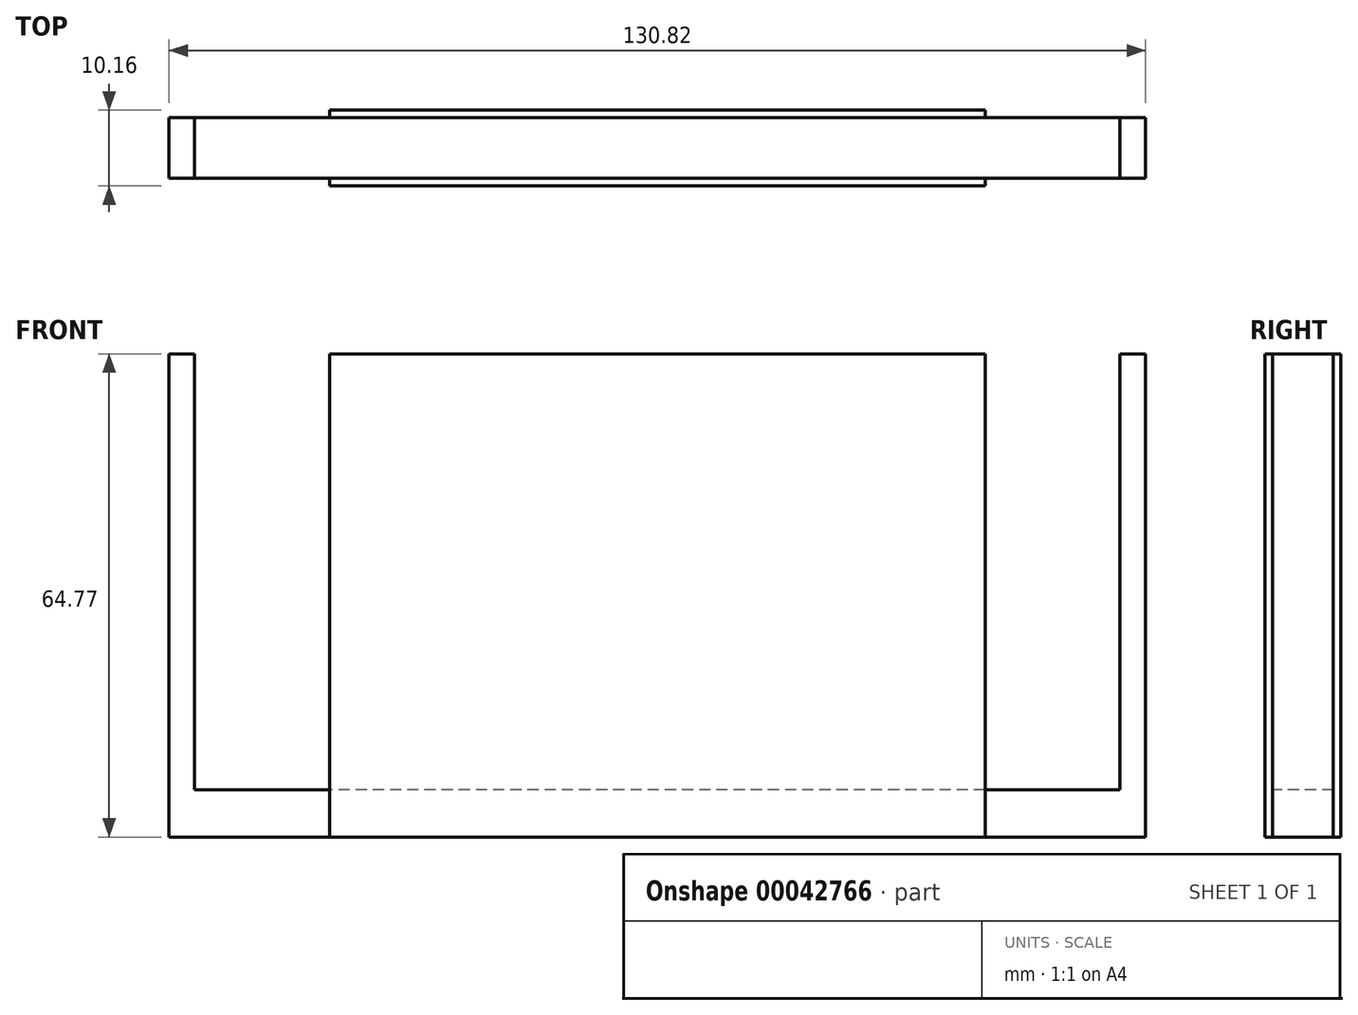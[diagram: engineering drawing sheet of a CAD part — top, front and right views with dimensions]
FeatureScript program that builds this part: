
annotation { "Feature Type Name" : "Feature", "Feature Type Description" : "" }
export const myFeature = defineFeature(function(context is Context, id is Id, definition is map)
    precondition{}
    {
        {
            var Q0;
            Q0=qCreatedBy(makeId("Top.planeOp"),FACE);
            var sketch = newSketch(context, id + "F0", { "sketchPlane" : qUnion([Q0])});
            skLineSegment(sketch, "E0.rect.bottom", {"start": v(61.98, 4.06) * mm, "end": v(-61.98, 4.06) * mm});
            skLineSegment(sketch, "E0.rect.top", {"start": v(61.98, -4.06) * mm, "end": v(-61.98, -4.06) * mm});
            skLineSegment(sketch, "E0.rect.left", {"start": v(61.98, 4.06) * mm, "end": v(61.98, -4.06) * mm});
            skLineSegment(sketch, "E0.rect.right", {"start": v(-61.98, 4.06) * mm, "end": v(-61.98, -4.06) * mm});
            skPoint(sketch, "E0.rect.middle", {"position": v(0, 0) * mm});
            skLineSegment(sketch, "E1.rect.bottom", {"start": v(43.9, 5.08) * mm, "end": v(-43.9, 5.08) * mm});
            skLineSegment(sketch, "E1.rect.top", {"start": v(43.9, -5.08) * mm, "end": v(-43.9, -5.08) * mm});
            skLineSegment(sketch, "E1.rect.left", {"start": v(43.9, 5.08) * mm, "end": v(43.9, -5.08) * mm});
            skLineSegment(sketch, "E1.rect.right", {"start": v(-43.9, 5.08) * mm, "end": v(-43.9, -5.08) * mm});
            skLineSegment(sketch, "E2.rect.bottom", {"start": v(65.41, 4.06) * mm, "end": v(-65.41, 4.06) * mm});
            skLineSegment(sketch, "E2.rect.top", {"start": v(65.41, -4.06) * mm, "end": v(-65.41, -4.06) * mm});
            skLineSegment(sketch, "E2.rect.left", {"start": v(65.41, 4.06) * mm, "end": v(65.41, -4.06) * mm});
            skLineSegment(sketch, "E2.rect.right", {"start": v(-65.41, 4.06) * mm, "end": v(-65.41, -4.06) * mm});
            skSolve(sketch);
        }
        {
            var Q0;
            {var subQ0=sQuery(id+"F0.wireOp",EDGE,"E0.rect.right");Q0=makeQuery(id+"F0.imprint","IMPRINT",FACE,{"disambiguationData":[TD([[makeQuery(id+"F0.imprint","IMPRINT",EDGE,{"derivedFrom":subQ0}),-1.0]])]});}
            var Q1;
            {var subQ0=sQuery(id+"F0.wireOp",EDGE,"E1.rect.bottom");Q1=makeQuery(id+"F0.imprint","IMPRINT",FACE,{"disambiguationData":[TD([[makeQuery(id+"F0.imprint","IMPRINT",EDGE,{"derivedFrom":subQ0}),1.0]])]});}
            var Q2;
            {var subQ0=sQuery(id+"F0.wireOp",EDGE,"E1.rect.top");Q2=makeQuery(id+"F0.imprint","IMPRINT",FACE,{"disambiguationData":[TD([[makeQuery(id+"F0.imprint","IMPRINT",EDGE,{"derivedFrom":subQ0}),-1.0]])]});}
            var Q3;
            {var subQ0=sQuery(id+"F0.wireOp",EDGE,"E0.rect.right");Q3=makeQuery(id+"F0.imprint","IMPRINT",FACE,{"disambiguationData":[TD([[makeQuery(id+"F0.imprint","IMPRINT",EDGE,{"derivedFrom":subQ0}),1.0]])]});}
            var Q4;
            {var subQ0=sQuery(id+"F0.wireOp",EDGE,"E0.rect.left");Q4=makeQuery(id+"F0.imprint","IMPRINT",FACE,{"disambiguationData":[TD([[makeQuery(id+"F0.imprint","IMPRINT",EDGE,{"derivedFrom":subQ0}),-1.0]])]});}
            var Q5;
            {var subQ0=sQuery(id+"F0.wireOp",EDGE,"E0.rect.left");Q5=makeQuery(id+"F0.imprint","IMPRINT",FACE,{"disambiguationData":[TD([[makeQuery(id+"F0.imprint","IMPRINT",EDGE,{"derivedFrom":subQ0}),1.0]])]});}
            var Q6;
            {var subQ0=sQuery(id+"F0.wireOp",EDGE,"E2.rect.bottom");var subQ1=sQuery(id+"F0.wireOp",EDGE,"E1.rect.left");var subQ2=makeQuery(id+"F0.imprint","INTERSECT",VERTEX,{"derivedFrom":[subQ1,subQ0]});Q6=makeQuery(id+"F0.imprint","IMPRINT",FACE,{"disambiguationData":[TD([[makeQuery(id+"F0.imprint","IMPRINT",EDGE,{"disambiguationData":[TD([[subQ2,-1.0]])],"derivedFrom":subQ1}),-1.0]])]});}
            extrude(context, id + "F1", {"entities" : qUnion([Q0, Q1, Q2, Q3, Q4, Q5, Q6]), "oppositeDirection" : true, "depth" : 6.35 * mm});
        }
        {
            var Q0;
            {var subQ0=sQuery(id+"F0.wireOp",EDGE,"E1.rect.bottom");Q0=makeQuery(id+"F0.imprint","IMPRINT",FACE,{"disambiguationData":[TD([[makeQuery(id+"F0.imprint","IMPRINT",EDGE,{"derivedFrom":subQ0}),1.0]])]});}
            var Q1;
            {var subQ0=sQuery(id+"F0.wireOp",EDGE,"E0.rect.right");Q1=makeQuery(id+"F0.imprint","IMPRINT",FACE,{"disambiguationData":[TD([[makeQuery(id+"F0.imprint","IMPRINT",EDGE,{"derivedFrom":subQ0}),-1.0]])]});}
            var Q2;
            {var subQ0=sQuery(id+"F0.wireOp",EDGE,"E0.rect.left");Q2=makeQuery(id+"F0.imprint","IMPRINT",FACE,{"disambiguationData":[TD([[makeQuery(id+"F0.imprint","IMPRINT",EDGE,{"derivedFrom":subQ0}),1.0]])]});}
            var Q3;
            {var subQ0=sQuery(id+"F0.wireOp",EDGE,"E1.rect.top");Q3=makeQuery(id+"F0.imprint","IMPRINT",FACE,{"disambiguationData":[TD([[makeQuery(id+"F0.imprint","IMPRINT",EDGE,{"derivedFrom":subQ0}),-1.0]])]});}
            extrude(context, id + "F2", {"entities" : qUnion([Q0, Q1, Q2, Q3]), "operationType" : NewBodyOperationType.ADD, "depth" : 58.42 * mm});
        }
    });
